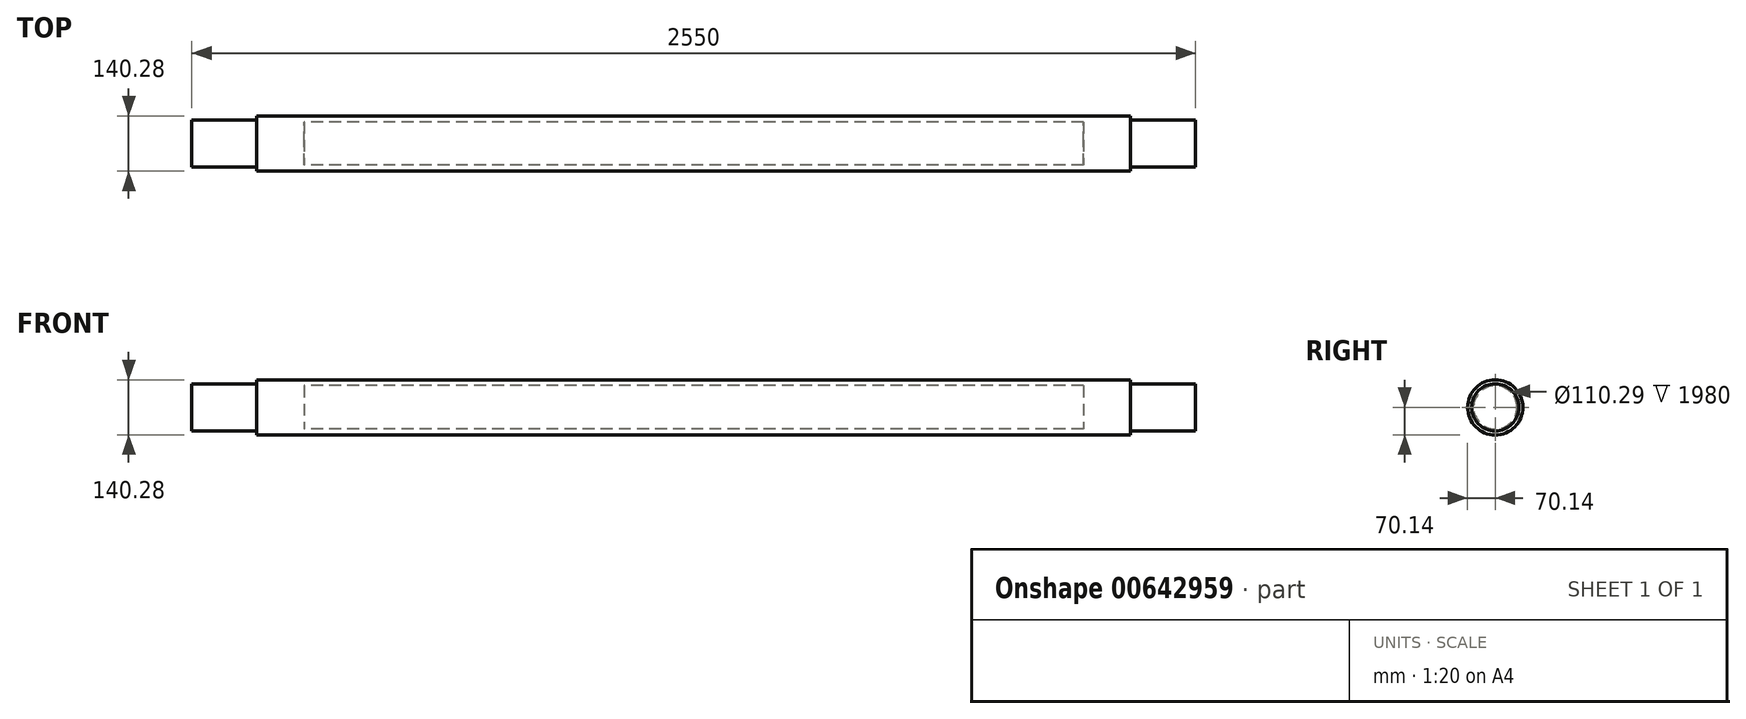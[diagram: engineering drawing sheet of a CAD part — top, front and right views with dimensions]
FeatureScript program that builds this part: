
annotation { "Feature Type Name" : "Feature", "Feature Type Description" : "" }
export const myFeature = defineFeature(function(context is Context, id is Id, definition is map)
    precondition{}
    {
        {
            var Q0;
            Q0=qCreatedBy(makeId("Front.planeOp"),FACE);
            var sketch = newSketch(context, id + "F0", { "sketchPlane" : qUnion([Q0])});
            skLineSegment(sketch, "E0", {"start": v(0, 0) * mm, "end": v(0, 70.14) * mm, "construction": true});
            skLineSegment(sketch, "E1", {"start": v(-1110, 70.14) * mm, "end": v(1110, 70.14) * mm});
            skLineSegment(sketch, "E2", {"start": v(-1110, 70.14) * mm, "end": v(-1110, 60) * mm});
            skLineSegment(sketch, "E3", {"start": v(-1110, 60) * mm, "end": v(-1275, 60) * mm});
            skLineSegment(sketch, "E4", {"start": v(-1275, 60) * mm, "end": v(-1275, 0) * mm});
            skLineSegment(sketch, "E5", {"start": v(-1275, 0) * mm, "end": v(-990, 0) * mm});
            skLineSegment(sketch, "E6", {"start": v(-990, 0) * mm, "end": v(-990, 55.14) * mm});
            skLineSegment(sketch, "E7", {"start": v(-990, 55.14) * mm, "end": v(990, 55.14) * mm});
            skLineSegment(sketch, "E8", {"start": v(990, 55.14) * mm, "end": v(990, 0) * mm});
            skLineSegment(sketch, "E9", {"start": v(990, 0) * mm, "end": v(1275, 0) * mm});
            skLineSegment(sketch, "E10", {"start": v(1275, 0) * mm, "end": v(1275, 60) * mm});
            skLineSegment(sketch, "E11", {"start": v(1275, 60) * mm, "end": v(1110, 60) * mm});
            skLineSegment(sketch, "E12", {"start": v(1110, 60) * mm, "end": v(1110, 70.14) * mm});
            skLineSegment(sketch, "E13", {"start": v(0, 0) * mm, "end": v(328.7, 0) * mm, "construction": true});
            skSolve(sketch);
        }
        {
            var Q0;
            Q0 = qSketchRegion(id + "F0", true);
            var Q1;
            Q1=sQuery(id+"F0.wireOp",EDGE,"E13");
            revolve(context, id + "F1", {"entities" : qUnion([Q0]), "axis" : qUnion([Q1]), "revolveType" : RevolveType.FULL});
        }
    });
